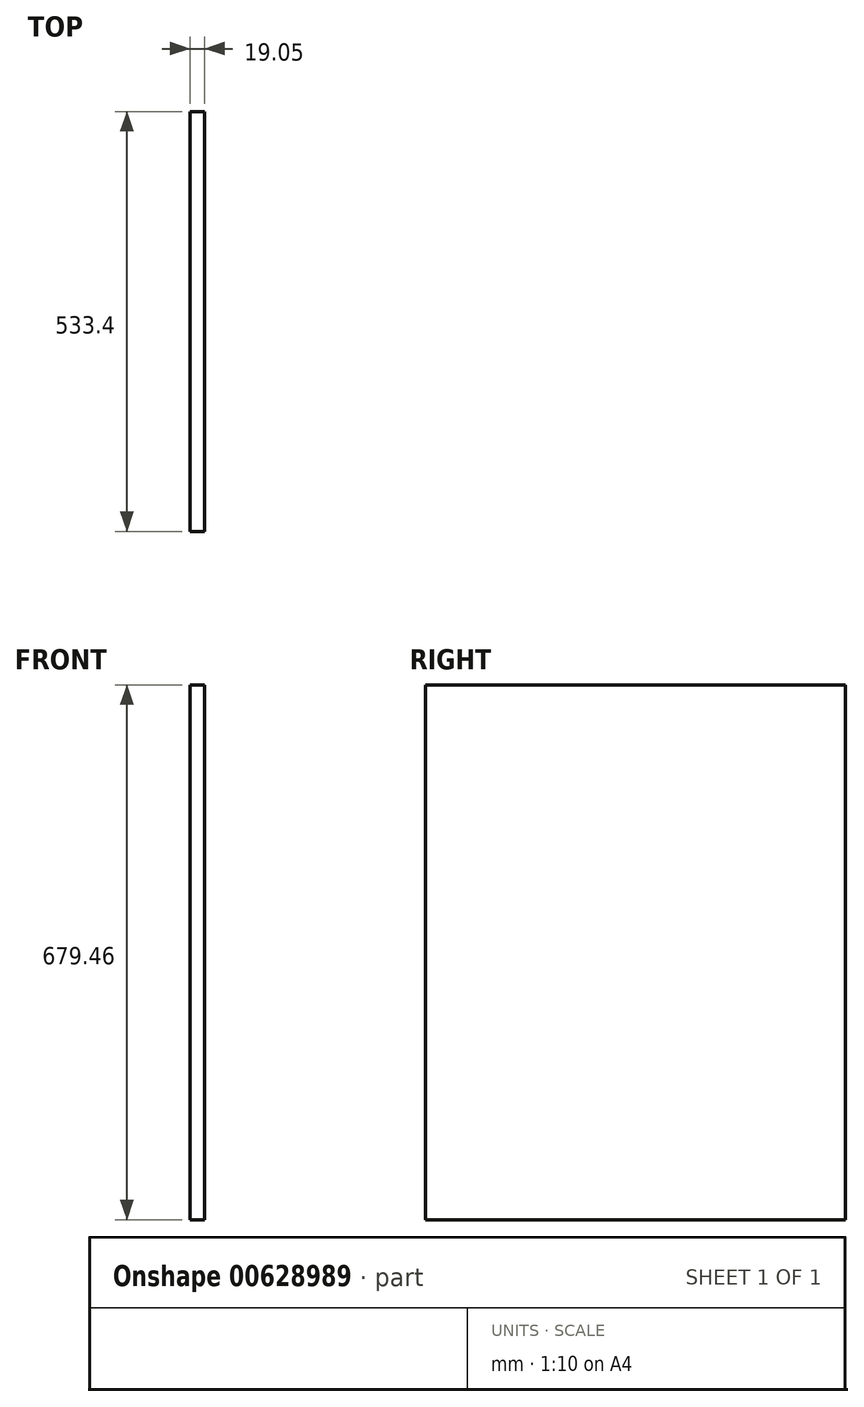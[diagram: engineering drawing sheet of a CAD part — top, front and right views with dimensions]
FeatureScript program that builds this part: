
annotation { "Feature Type Name" : "Feature", "Feature Type Description" : "" }
export const myFeature = defineFeature(function(context is Context, id is Id, definition is map)
    precondition{}
    {
        {
            var Q0;
            Q0=qCreatedBy(makeId("Right.planeOp"),FACE);
            var sketch = newSketch(context, id + "F0", { "sketchPlane" : qUnion([Q0])});
            skLineSegment(sketch, "E0.bottom", {"start": v(266.7, 339.73) * mm, "end": v(-266.7, 339.73) * mm});
            skLineSegment(sketch, "E0.top", {"start": v(266.7, -339.73) * mm, "end": v(-266.7, -339.73) * mm});
            skLineSegment(sketch, "E0.left", {"start": v(266.7, 339.73) * mm, "end": v(266.7, -339.73) * mm});
            skLineSegment(sketch, "E0.right", {"start": v(-266.7, 339.73) * mm, "end": v(-266.7, -339.73) * mm});
            skPoint(sketch, "E0.middle", {"position": v(0, 0) * mm});
            skSolve(sketch);
        }
        {
            var Q0;
            Q0=makeQuery(id+"F0.imprint","IMPRINT",FACE,{"disambiguationData":[TD([[makeQuery(id+"F0.imprint","IMPRINT",EDGE,{"derivedFrom":sQuery(id+"F0.wireOp",EDGE,"E0.bottom")}),1.0]])]});
            extrude(context, id + "F1", {"entities" : qUnion([Q0]), "depth" : 19.05 * mm, "offsetDistance" : 25.4 * mm});
        }
    });
